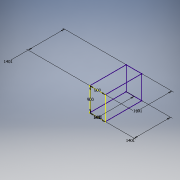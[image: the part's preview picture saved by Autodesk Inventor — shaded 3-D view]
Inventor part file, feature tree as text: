
AUTODESK INVENTOR PART (.ipt)
format: ipt  version: 2016 (Build 200138000, 138)  size: 93,184 bytes
history: native  units: mm
features: sketch x2
ambient origin geometry x8: Origin, YZ Plane, XZ Plane, XY Plane, X Axis, Y Axis, Z Axis, Center Point
feature tree (2):
  sketch  "Boceto1"  dims[d1=600.0mm]
  sketch  "Boceto 3D2"  dims[d2=900.0mm d3=600.0mm d4=1401.0mm d5=1401.0mm d6=1401.0mm d7=1401.0mm]
